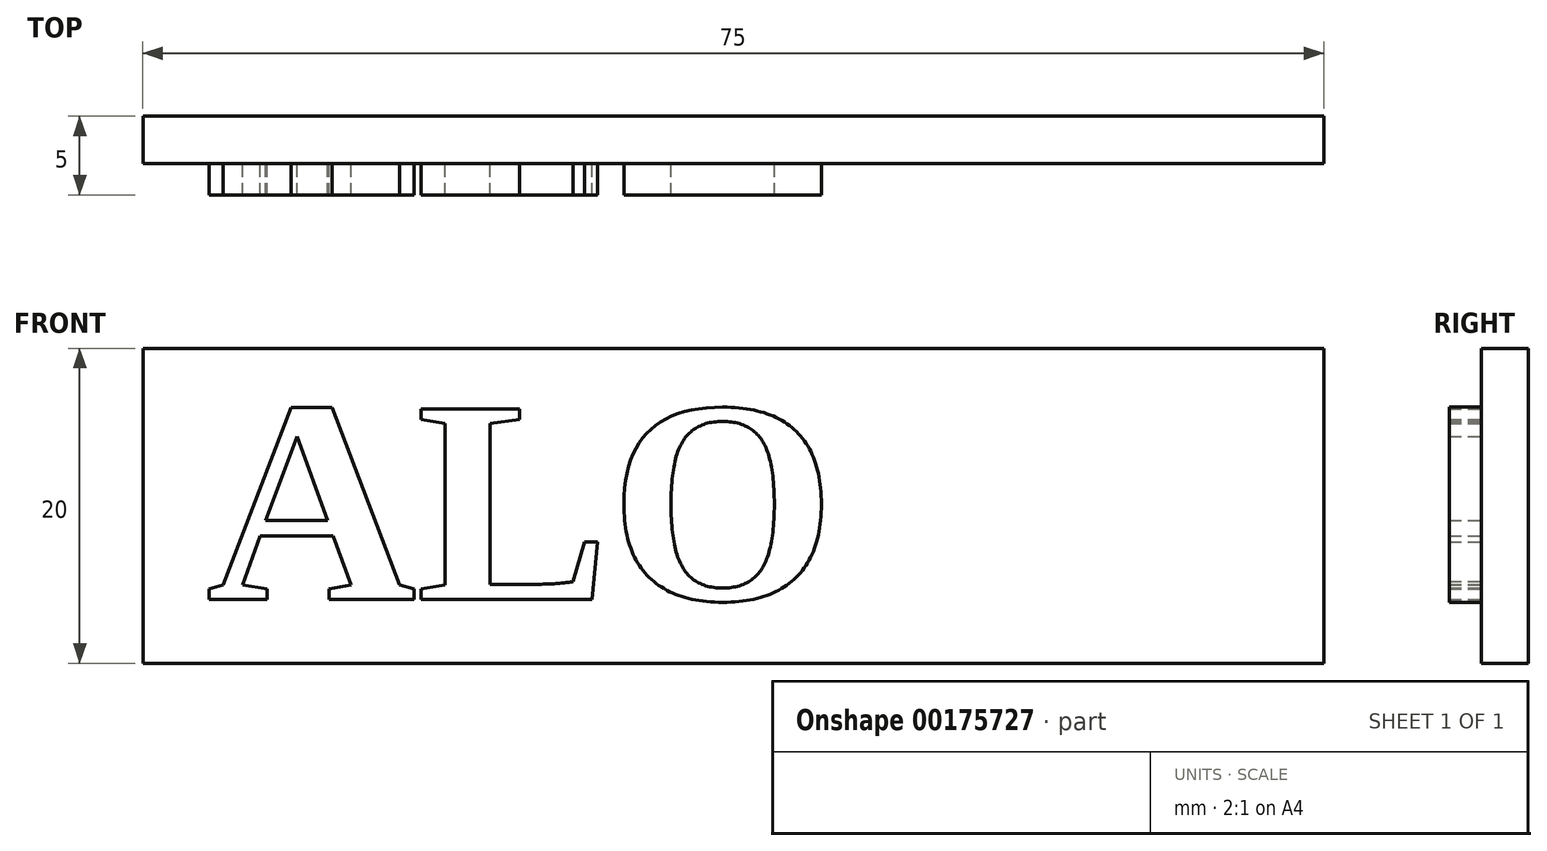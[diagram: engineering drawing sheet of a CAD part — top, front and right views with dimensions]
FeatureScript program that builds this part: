
annotation { "Feature Type Name" : "Feature", "Feature Type Description" : "" }
export const myFeature = defineFeature(function(context is Context, id is Id, definition is map)
    precondition{}
    {
        {
            var Q0;
            Q0=qCreatedBy(makeId("Front.planeOp"),FACE);
            var sketch = newSketch(context, id + "F0", { "sketchPlane" : qUnion([Q0])});
            skLineSegment(sketch, "E0.bottom", {"start": v(-0.05, -0.13) * mm, "end": v(74.95, -0.13) * mm});
            skLineSegment(sketch, "E0.top", {"start": v(-0.05, -20.13) * mm, "end": v(74.95, -20.13) * mm});
            skLineSegment(sketch, "E0.left", {"start": v(-0.05, -0.13) * mm, "end": v(-0.05, -20.13) * mm});
            skLineSegment(sketch, "E0.right", {"start": v(74.95, -0.13) * mm, "end": v(74.95, -20.13) * mm});
            skSolve(sketch);
        }
        {
            var Q0;
            Q0=makeQuery(id+"F0.imprint","IMPRINT",FACE,{"disambiguationData":[TD([[makeQuery(id+"F0.imprint","IMPRINT",EDGE,{"derivedFrom":sQuery(id+"F0.wireOp",EDGE,"E0.bottom")}),-1.0]])]});
            extrude(context, id + "F1", {"entities" : qUnion([Q0]), "depth" : 3 * mm});
        }
        {
            var Q0;
            Q0=makeQuery(id+"F1.opExtrude","CAP_FACE",FACE,{"disambiguationData":[OSD([sQuery(id+"F0.wireOp",EDGE,"E0.bottom"),sQuery(id+"F0.wireOp",EDGE,"E0.top"),sQuery(id+"F0.wireOp",EDGE,"E0.left"),sQuery(id+"F0.wireOp",EDGE,"E0.right")])],"isStart":false});
            var sketch = newSketch(context, id + "F2", { "sketchPlane" : qUnion([Q0])});
            skText(sketch, "E1", { "text": "ALO", "fontName": "Tinos-Bold.ttf"});
            const initialGuessF2  = {"E1": [0.00398, -0.01607, 1, 0, 0.01328]};
            skSetInitialGuess(sketch, initialGuessF2);
            skSolve(sketch);
        }
        {
            var Q0;
            Q0 = qSketchRegion(id + "F2", true);
            extrude(context, id + "F3", {"entities" : qUnion([Q0]), "operationType" : NewBodyOperationType.ADD, "depth" : 2 * mm});
        }
    });
